# Revit family: Table Lamp - Arm Extension
name_source: partatom
category: Lighting Fixtures
revit_build: Autodesk Revit Architecture 2012 (Build: 20110210_1515)
units: mm (PartAtom-declared; Revit-internal decimal feet)

## types (4) — shared parameters
Assembly Code = D5020220
Ballast Number of Poles = 1
Base MaterialStand = Metal - Chrome
Color Filter = 16777215
Dimming Lamp Color Temperature Shift = <None>
Load Classification = Lighting - Dwelling Unit
Shade Material = Metal - Chrome
Spot Beam Angle = 30.00°
Spot Field Angle = 90.00°

## per-type parameters (varying)
| type | Apparent Load | Ballast Voltage | Lamp | Light Source Symbol Length | Tilt Angle |
| 100W - 277V | 100 VA | 277 V | R-30 | 10' - 0" | 60.00° |
| 60W - 120V | 60 VA | 120 V | A-19 | 10' - 0" | 60.00° |
| 60W - 277V | 60 VA | 277 V | A-19 | 10' - 0" | 60.00° |
| 100W - 120V | 100 VA | 120 V | R-30 | 4' - 0" | 45.00° |

## geometry (parser evidence)
native form markers: Sweep x1
no freeform markers — native parametric forms only
